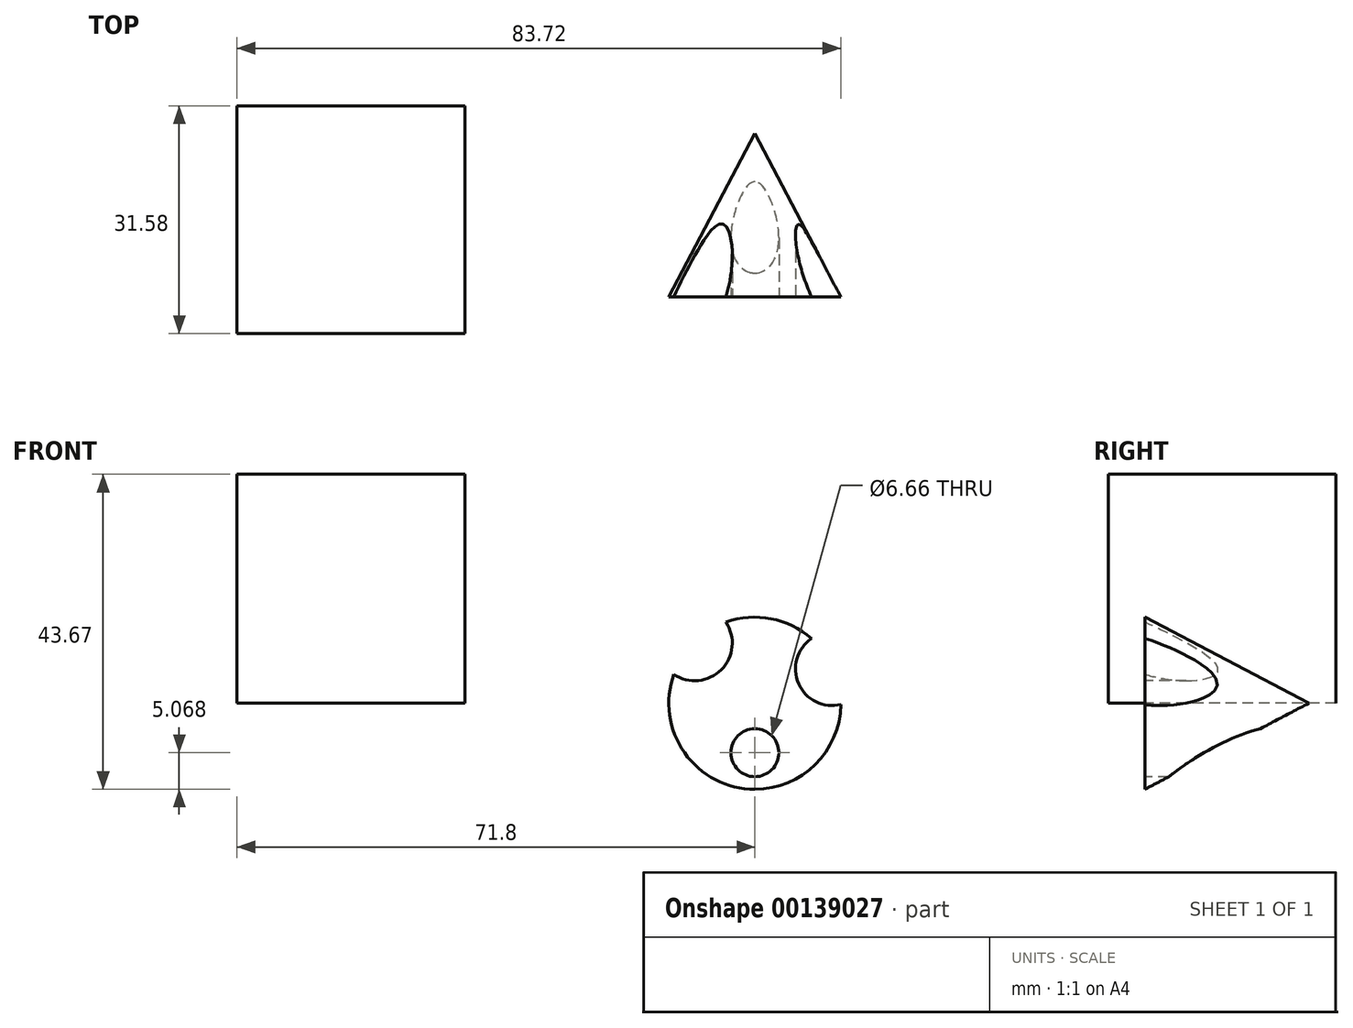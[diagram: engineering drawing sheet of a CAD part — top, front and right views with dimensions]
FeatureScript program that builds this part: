
annotation { "Feature Type Name" : "Feature", "Feature Type Description" : "" }
export const myFeature = defineFeature(function(context is Context, id is Id, definition is map)
    precondition{}
    {
        {
            var Q0;
            Q0=qCreatedBy(makeId("Top.planeOp"),FACE);
            var sketch = newSketch(context, id + "F0", { "sketchPlane" : qUnion([Q0])});
            skLineSegment(sketch, "E0.bottom", {"start": v(-40.22, 56.3) * mm, "end": v(-71.8, 56.3) * mm});
            skLineSegment(sketch, "E0.top", {"start": v(-40.22, 24.73) * mm, "end": v(-71.8, 24.73) * mm});
            skLineSegment(sketch, "E0.left", {"start": v(-40.22, 56.3) * mm, "end": v(-40.22, 24.73) * mm});
            skLineSegment(sketch, "E0.right", {"start": v(-71.8, 56.3) * mm, "end": v(-71.8, 24.73) * mm});
            skPoint(sketch, "E0.middle", {"position": v(-56.01, 40.52) * mm});
            skSolve(sketch);
        }
        {
            var Q0;
            Q0=makeQuery(id+"F0.imprint","IMPRINT",FACE,{"disambiguationData":[TD([[makeQuery(id+"F0.imprint","IMPRINT",EDGE,{"derivedFrom":sQuery(id+"F0.wireOp",EDGE,"E0.bottom")}),1.0]])]});
            extrude(context, id + "F1", {"entities" : qUnion([Q0]), "depth" : 31.75 * mm});
        }
        {
            var Q0;
            Q0=qCreatedBy(makeId("Top.planeOp"),FACE);
            var sketch = newSketch(context, id + "F2", { "sketchPlane" : qUnion([Q0])});
            skLineSegment(sketch, "E1", {"start": v(0, 52.5) * mm, "end": v(0, 29.81) * mm});
            skLineSegment(sketch, "E2", {"start": v(0, 29.81) * mm, "end": v(11.92, 29.81) * mm});
            skLineSegment(sketch, "E3", {"start": v(11.92, 29.81) * mm, "end": v(0, 52.5) * mm});
            skSolve(sketch);
        }
        {
            var Q0;
            Q0 = qSketchRegion(id + "F2", true);
            var Q1;
            Q1=sQuery(id+"F2.wireOp",EDGE,"E1");
            revolve(context, id + "F3", {"entities" : qUnion([Q0]), "axis" : qUnion([Q1]), "revolveType" : RevolveType.FULL});
        }
        {
            var Q0;
            Q0=qCreatedBy(makeId("Front.planeOp"),FACE);
            cPlane(context, id + "F4", {"entities" : qUnion([Q0]), "cplaneType" : CPlaneType.OFFSET, "offset" : 25.4 * mm, "width" : 152.4 * mm, "height" : 152.4 * mm});
        }
        {
            var Q0;
            Q0=qCreatedBy(id+"F4.planeOp",FACE);
            var sketch = newSketch(context, id + "F5", { "sketchPlane" : qUnion([Q0])});
            skCircle(sketch, "E4", {"center": v(-8.34, 8.34) * mm, "radius": 5.21 * mm});
            skCircle(sketch, "E5", {"center": v(10.73, 4.77) * mm, "radius": 5.1 * mm});
            skCircle(sketch, "E6", {"center": v(0, -6.85) * mm, "radius": 3.33 * mm});
            skSolve(sketch);
        }
        {
            var Q0;
            Q0 = qSketchRegion(id + "F5", true);
            extrude(context, id + "F6", {"entities" : qUnion([Q0]), "operationType" : NewBodyOperationType.REMOVE, "endBound" : BoundingType.THROUGH_ALL, "oppositeDirection" : true, "depth" : 25.4 * mm});
        }
    });
